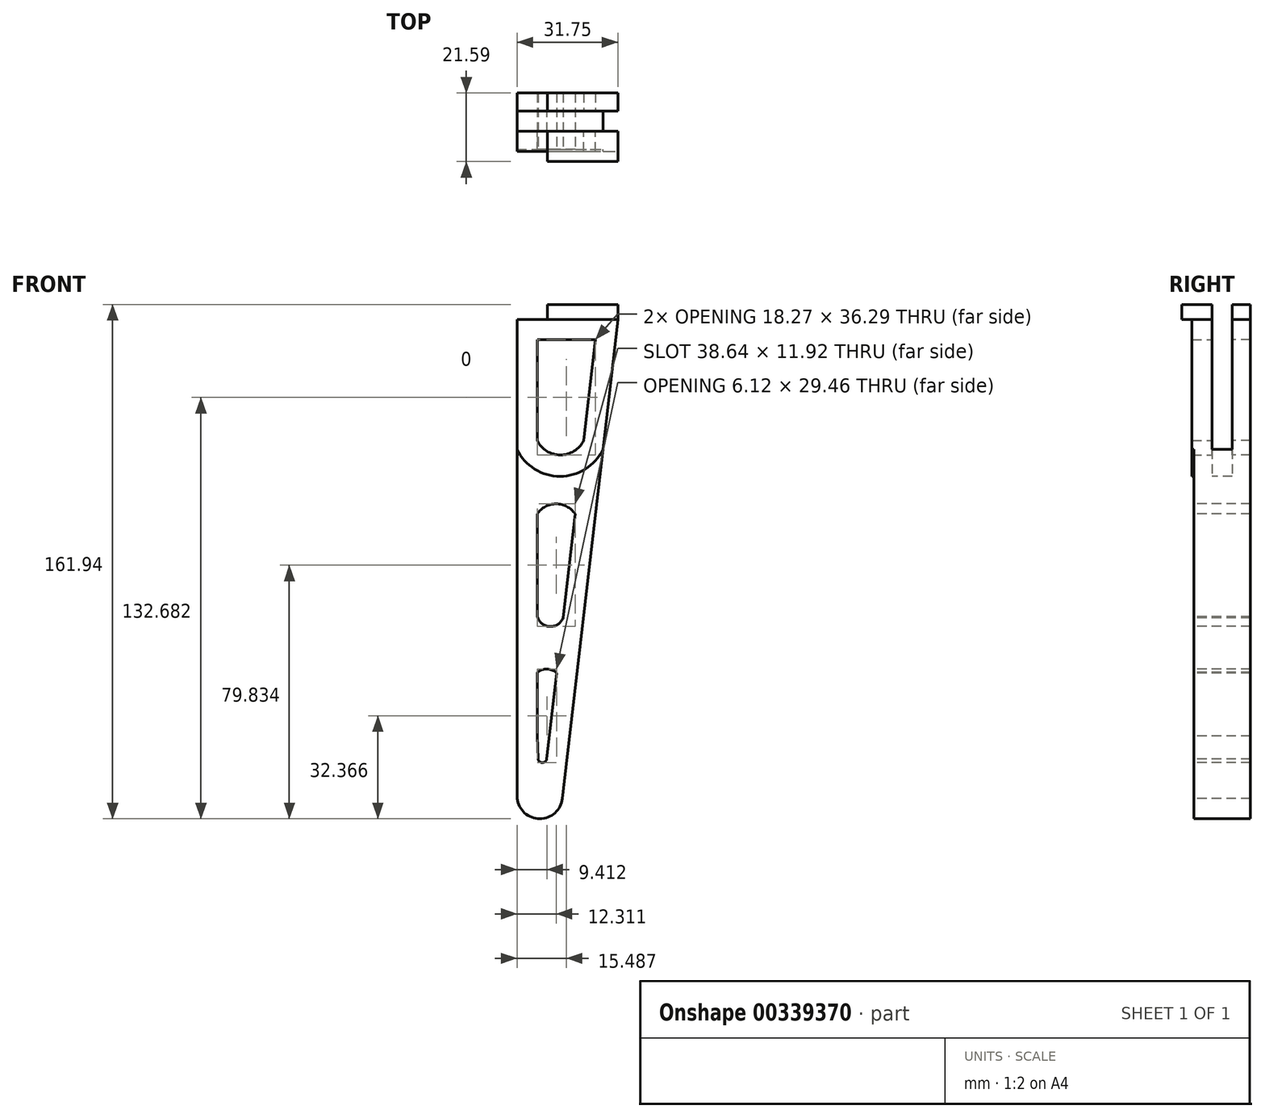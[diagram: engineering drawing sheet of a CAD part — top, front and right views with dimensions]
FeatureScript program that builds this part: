
annotation { "Feature Type Name" : "Feature", "Feature Type Description" : "" }
export const myFeature = defineFeature(function(context is Context, id is Id, definition is map)
    precondition{}
    {
        {
            var Q0;
            Q0=qCreatedBy(makeId("Front.planeOp"),FACE);
            var sketch = newSketch(context, id + "F0", { "sketchPlane" : qUnion([Q0])});
            skLineSegment(sketch, "E0", {"start": v(-10.93, 0) * mm, "end": v(-10.93, 75.4) * mm});
            skLineSegment(sketch, "E1.MirrorCS", {"start": v(-10.93, 0) * mm, "end": v(-10.93, -75.4) * mm});
            skLineSegment(sketch, "E2", {"start": v(-10.93, 75.4) * mm, "end": v(20.82, 75.4) * mm});
            skLineSegment(sketch, "E3", {"start": v(3.36, -75.4) * mm, "end": v(20.82, 75.4) * mm});
            skArc(sketch, "E4", {"start": v(-10.93, -75.4) * mm, "mid": v(-3.79, -81.77) * mm, "end": v(3.36, -75.4) * mm});
            skLineSegment(sketch, "E5", {"start": v(20.82, 75.4) * mm, "end": v(20.82, 80.17) * mm});
            skLineSegment(sketch, "E6", {"start": v(20.82, 80.17) * mm, "end": v(-1.4, 80.17) * mm});
            skLineSegment(sketch, "E7", {"start": v(-1.4, 80.17) * mm, "end": v(-1.4, 75.4) * mm});
            skLineSegment(sketch, "E8.0", {"start": v(-0.78, -55.94) * mm, "end": v(1.54, -35.87) * mm});
            skLineSegment(sketch, "E8.1", {"start": v(-4.58, 69.06) * mm, "end": v(13.7, 69.06) * mm});
            skLineSegment(sketch, "E8.3", {"start": v(-4.58, 0) * mm, "end": v(-4.58, -18.1) * mm});
            skLineSegment(sketch, "E8.4", {"start": v(-4.58, 0) * mm, "end": v(-4.58, 14.2) * mm});
            skLineSegment(sketch, "E9", {"start": v(-4.58, 69.06) * mm, "end": v(-4.58, 37.3) * mm});
            skArc(sketch, "E10", {"start": v(-4.58, 37.3) * mm, "mid": v(2.72, 32.77) * mm, "end": v(10.02, 37.3) * mm});
            skLineSegment(sketch, "E11.trimOffspring", {"start": v(-4.58, 37.3) * mm, "end": v(-4.58, 69.06) * mm});
            skLineSegment(sketch, "E12.trimOffspring", {"start": v(10.02, 37.3) * mm, "end": v(13.7, 69.06) * mm});
            skArc(sketch, "E13", {"start": v(7.34, 14.2) * mm, "mid": v(1.38, 17.38) * mm, "end": v(-4.58, 14.2) * mm});
            skPoint(sketch, "E13.startSnap0", {"position": v(-4.58, 14.2) * mm});
            skPoint(sketch, "E14.orphan", {"position": v(-4.58, 28.4) * mm});
            skLineSegment(sketch, "E15", {"start": v(-0.78, -55.94) * mm, "end": v(-1.6, -62.95) * mm});
            skLineSegment(sketch, "E16", {"start": v(-4.36, -62.94) * mm, "end": v(-4.58, -55.76) * mm});
            skArc(sketch, "E17", {"start": v(-4.58, -18.1) * mm, "mid": v(-0.7, -21.26) * mm, "end": v(3.55, -18.59) * mm});
            skArc(sketch, "E18", {"start": v(1.54, -35.87) * mm, "mid": v(-1.49, -34.67) * mm, "end": v(-4.58, -35.72) * mm});
            skArc(sketch, "E19", {"start": v(-4.36, -62.94) * mm, "mid": v(-2.98, -64.13) * mm, "end": v(-1.6, -62.95) * mm});
            skLineSegment(sketch, "E20.trimOffspring", {"start": v(-4.58, -35.72) * mm, "end": v(-4.58, -55.76) * mm});
            skLineSegment(sketch, "E21.trimOffspring", {"start": v(3.55, -18.59) * mm, "end": v(7.34, 14.2) * mm});
            skArc(sketch, "E22", {"start": v(-10.93, 34.5) * mm, "mid": v(2.58, 26.06) * mm, "end": v(16.08, 34.5) * mm});
            skSolve(sketch);
        }
        {
            var Q0;
            {var subQ0=sQuery(id+"F0.wireOp",EDGE,"E1.MirrorCS");Q0=makeQuery(id+"F0.imprint","IMPRINT",FACE,{"disambiguationData":[TD([[makeQuery(id+"F0.imprint","IMPRINT",EDGE,{"derivedFrom":subQ0}),1.0]])]});}
            extrude(context, id + "F1", {"entities" : qUnion([Q0]), "oppositeDirection" : true, "depth" : 8.9 * mm, "hasSecondDirection" : true, "secondDirectionOppositeDirection" : false, "secondDirectionDepth" : 6.35 * mm});
        }
        {
            var Q0;
            Q0=makeQuery(id+"F0.imprint","IMPRINT",FACE,{"disambiguationData":[TD([[makeQuery(id+"F0.imprint","IMPRINT",EDGE,{"derivedFrom":sQuery(id+"F0.wireOp",EDGE,"E8.1")}),1.0]])]});
            extrude(context, id + "F2", {"entities" : qUnion([Q0]), "operationType" : NewBodyOperationType.ADD, "depth" : 9.52 * mm, "hasSecondDirection" : true, "secondDirectionOppositeDirection" : false, "secondDirectionDepth" : 3.17 * mm});
        }
        {
            var Q0;
            {var subQ0=sQuery(id+"F0.wireOp",EDGE,"E5");Q0=makeQuery(id+"F0.imprint","IMPRINT",FACE,{"disambiguationData":[TD([[makeQuery(id+"F0.imprint","IMPRINT",EDGE,{"derivedFrom":subQ0}),1.0]])]});}
            var Q1;
            Q1=makeQuery(id+"F2.opExtrude","CAP_FACE",FACE,{"disambiguationData":[OSD([sQuery(id+"F0.wireOp",EDGE,"E0"),sQuery(id+"F0.wireOp",EDGE,"E2"),sQuery(id+"F0.wireOp",EDGE,"E3"),sQuery(id+"F0.wireOp",EDGE,"E8.1"),sQuery(id+"F0.wireOp",EDGE,"E10"),sQuery(id+"F0.wireOp",EDGE,"E11.trimOffspring"),sQuery(id+"F0.wireOp",EDGE,"E12.trimOffspring"),sQuery(id+"F0.wireOp",EDGE,"E22")])],"isStart":true});
            var Q2;
            Q2=makeQuery(id+"F2.opExtrude","CAP_FACE",FACE,{"disambiguationData":[OSD([sQuery(id+"F0.wireOp",EDGE,"E0"),sQuery(id+"F0.wireOp",EDGE,"E2"),sQuery(id+"F0.wireOp",EDGE,"E3"),sQuery(id+"F0.wireOp",EDGE,"E8.1"),sQuery(id+"F0.wireOp",EDGE,"E10"),sQuery(id+"F0.wireOp",EDGE,"E11.trimOffspring"),sQuery(id+"F0.wireOp",EDGE,"E12.trimOffspring"),sQuery(id+"F0.wireOp",EDGE,"E22")])],"isStart":true});
            extrude(context, id + "F3", {"entities" : qUnion([Q0]), "operationType" : NewBodyOperationType.ADD, "endBoundEntityFace" : qUnion([Q1]), "depth" : 12.7 * mm, "hasSecondDirection" : true, "secondDirectionBound" : SecondDirectionBoundingType.UP_TO_SURFACE, "secondDirectionOppositeDirection" : false, "secondDirectionBoundEntityFace" : qUnion([Q2]), "secondDirectionDepth" : 12.7 * mm});
        }
        {
            var Q0;
            Q0=makeQuery(id+"F1.opExtrude","SWEPT_BODY",BODY,{"disambiguationData":[OSD([sQuery(id+"F0.wireOp",EDGE,"E0"),sQuery(id+"F0.wireOp",EDGE,"E1.MirrorCS"),sQuery(id+"F0.wireOp",EDGE,"E3"),sQuery(id+"F0.wireOp",EDGE,"E4"),sQuery(id+"F0.wireOp",EDGE,"E8.0"),sQuery(id+"F0.wireOp",EDGE,"E8.3"),sQuery(id+"F0.wireOp",EDGE,"E8.4"),sQuery(id+"F0.wireOp",EDGE,"E13"),sQuery(id+"F0.wireOp",EDGE,"E15"),sQuery(id+"F0.wireOp",EDGE,"E16"),sQuery(id+"F0.wireOp",EDGE,"E17"),sQuery(id+"F0.wireOp",EDGE,"E18"),sQuery(id+"F0.wireOp",EDGE,"E19"),sQuery(id+"F0.wireOp",EDGE,"E20.trimOffspring"),sQuery(id+"F0.wireOp",EDGE,"E21.trimOffspring"),sQuery(id+"F0.wireOp",EDGE,"E22")])]});
            var Q1;
            Q1=qCreatedBy(makeId("Front.planeOp"),FACE);
            mirror(context, id + "F4", {"operationType" : NewBodyOperationType.ADD, "entities" : qUnion([Q0]), "mirrorPlane" : qUnion([Q1])});
        }
        {
            var Q0;
            Q0=makeQuery(id+"F4.opPattern","COPY",FACE,{"derivedFrom":makeQuery(id+"F2.opExtrude","CAP_FACE",FACE,{"disambiguationData":[OSD([sQuery(id+"F0.wireOp",EDGE,"E0"),sQuery(id+"F0.wireOp",EDGE,"E2"),sQuery(id+"F0.wireOp",EDGE,"E3"),sQuery(id+"F0.wireOp",EDGE,"E8.1"),sQuery(id+"F0.wireOp",EDGE,"E10"),sQuery(id+"F0.wireOp",EDGE,"E11.trimOffspring"),sQuery(id+"F0.wireOp",EDGE,"E12.trimOffspring"),sQuery(id+"F0.wireOp",EDGE,"E22")])],"isStart":false}),"instanceName":"1"});
            var Q1;
            Q1=makeQuery(id+"F4.opPattern","COPY",FACE,{"derivedFrom":makeQuery(id+"F3.opExtrude","CAP_FACE",FACE,{"disambiguationData":[OSD([sQuery(id+"F0.wireOp",EDGE,"E2"),sQuery(id+"F0.wireOp",EDGE,"E5"),sQuery(id+"F0.wireOp",EDGE,"E6"),sQuery(id+"F0.wireOp",EDGE,"E7")])],"isStart":false}),"instanceName":"1"});
            var Q2;
            Q2=makeQuery(id+"F1.opExtrude","CAP_FACE",FACE,{"disambiguationData":[OSD([sQuery(id+"F0.wireOp",EDGE,"E0"),sQuery(id+"F0.wireOp",EDGE,"E1.MirrorCS"),sQuery(id+"F0.wireOp",EDGE,"E3"),sQuery(id+"F0.wireOp",EDGE,"E4"),sQuery(id+"F0.wireOp",EDGE,"E8.0"),sQuery(id+"F0.wireOp",EDGE,"E8.3"),sQuery(id+"F0.wireOp",EDGE,"E8.4"),sQuery(id+"F0.wireOp",EDGE,"E13"),sQuery(id+"F0.wireOp",EDGE,"E15"),sQuery(id+"F0.wireOp",EDGE,"E16"),sQuery(id+"F0.wireOp",EDGE,"E17"),sQuery(id+"F0.wireOp",EDGE,"E18"),sQuery(id+"F0.wireOp",EDGE,"E19"),sQuery(id+"F0.wireOp",EDGE,"E20.trimOffspring"),sQuery(id+"F0.wireOp",EDGE,"E21.trimOffspring"),sQuery(id+"F0.wireOp",EDGE,"E22")])],"isStart":false});
            extrude(context, id + "F5", {"entities" : qUnion([Q0, Q1]), "operationType" : NewBodyOperationType.REMOVE, "endBound" : BoundingType.UP_TO_SURFACE, "oppositeDirection" : true, "endBoundEntityFace" : qUnion([Q2]), "depth" : 25.4 * mm});
        }
    });
